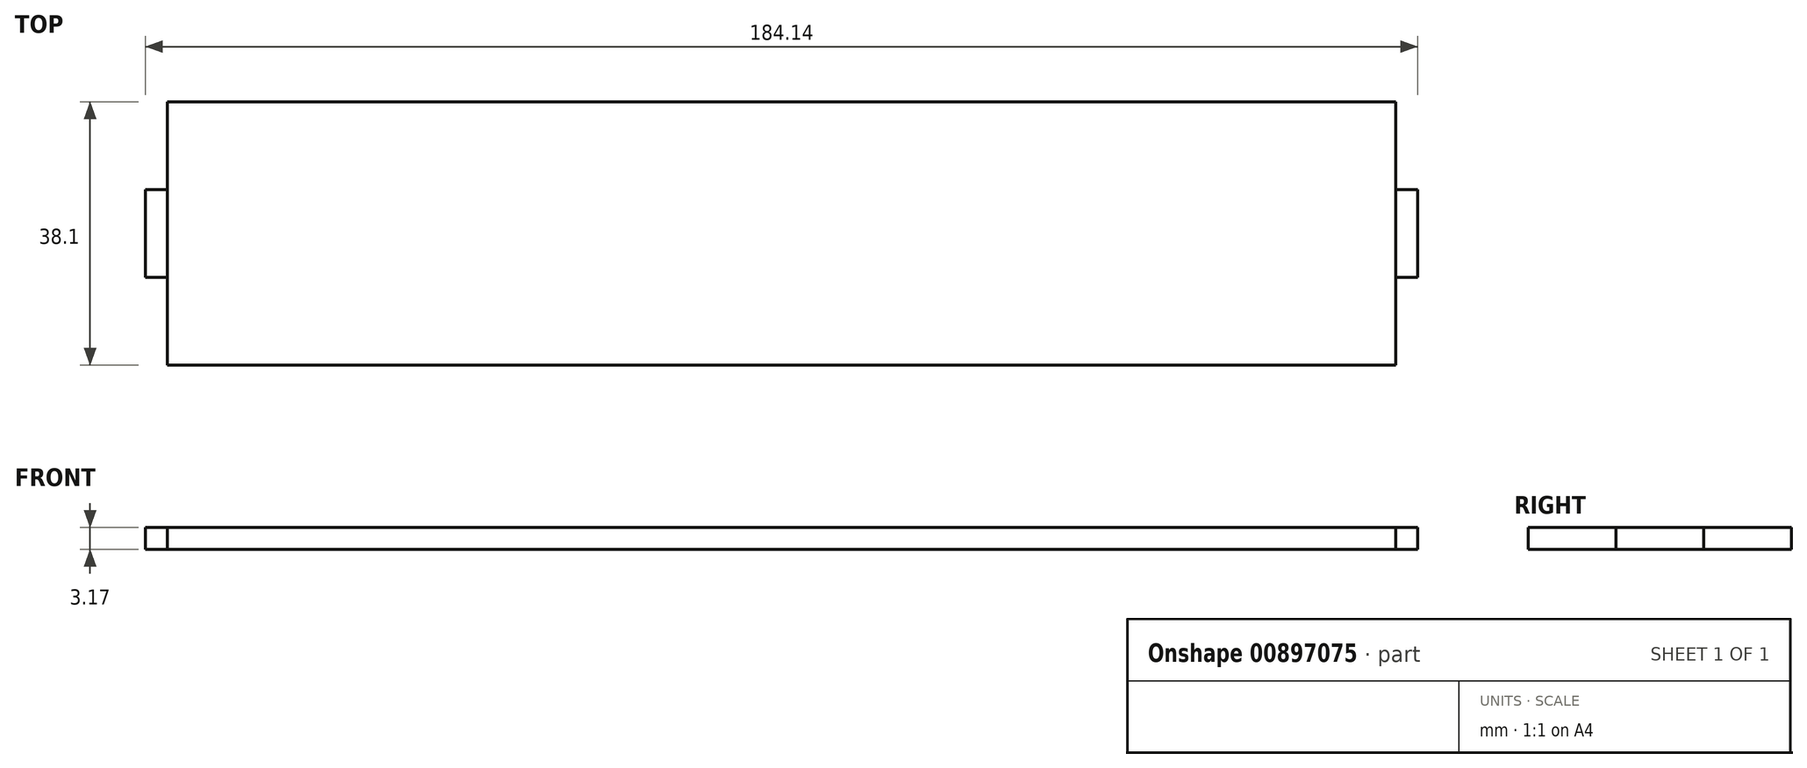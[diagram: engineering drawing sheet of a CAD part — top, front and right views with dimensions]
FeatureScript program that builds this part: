
annotation { "Feature Type Name" : "Feature", "Feature Type Description" : "" }
export const myFeature = defineFeature(function(context is Context, id is Id, definition is map)
    precondition{}
    {
        {
            var Q0;
            Q0=qCreatedBy(makeId("Top.planeOp"),FACE);
            var sketch = newSketch(context, id + "F0", { "sketchPlane" : qUnion([Q0])});
            skLineSegment(sketch, "E0.bottom", {"start": v(0, 0) * mm, "end": v(-177.8, 0) * mm});
            skLineSegment(sketch, "E0.top", {"start": v(0, -38.1) * mm, "end": v(-177.8, -38.1) * mm});
            skLineSegment(sketch, "E0.left", {"start": v(0, 0) * mm, "end": v(0, -38.1) * mm});
            skLineSegment(sketch, "E0.right", {"start": v(-177.8, 0) * mm, "end": v(-177.8, -38.1) * mm});
            skSolve(sketch);
        }
        {
            var Q0;
            Q0=makeQuery(id+"F0.imprint","IMPRINT",FACE,{"disambiguationData":[TD([[makeQuery(id+"F0.imprint","IMPRINT",EDGE,{"derivedFrom":sQuery(id+"F0.wireOp",EDGE,"E0.bottom")}),1.0]])]});
            var sketch = newSketch(context, id + "F1", { "sketchPlane" : qUnion([Q0])});
            skLineSegment(sketch, "E1.bottom", {"start": v(0, -12.7) * mm, "end": v(3.18, -12.7) * mm});
            skLineSegment(sketch, "E1.top", {"start": v(0, -25.4) * mm, "end": v(3.18, -25.4) * mm});
            skLineSegment(sketch, "E1.left", {"start": v(0, -12.7) * mm, "end": v(0, -25.4) * mm});
            skLineSegment(sketch, "E1.right", {"start": v(3.18, -12.7) * mm, "end": v(3.18, -25.4) * mm});
            skSolve(sketch);
        }
        {
            var Q0;
            {var subQ2=sQuery(id+"F1.wireOp",EDGE,"E1.left");Q0=makeQuery(id+"F1.imprint","IMPRINT",FACE,{"disambiguationData":[TD([[makeQuery(id+"F1.imprint","IMPRINT",EDGE,{"derivedFrom":subQ2}),-1.0]])]});}
            var sketch = newSketch(context, id + "F2", { "sketchPlane" : qUnion([Q0])});
            skLineSegment(sketch, "E2.bottom", {"start": v(-177.8, -25.4) * mm, "end": v(-180.98, -25.4) * mm});
            skLineSegment(sketch, "E2.top", {"start": v(-177.8, -12.7) * mm, "end": v(-180.98, -12.7) * mm});
            skLineSegment(sketch, "E2.left", {"start": v(-177.8, -25.4) * mm, "end": v(-177.8, -12.7) * mm});
            skLineSegment(sketch, "E2.right", {"start": v(-180.98, -25.4) * mm, "end": v(-180.98, -12.7) * mm});
            skSolve(sketch);
        }
        {
            var Q0;
            Q0 = qSketchRegion(id + "F0", true);
            var Q1;
            Q1 = qSketchRegion(id + "F1", true);
            var Q2;
            Q2 = qSketchRegion(id + "F2", true);
            extrude(context, id + "F3", {"entities" : qUnion([Q0, Q1, Q2]), "depth" : 3.17 * mm, "offsetDistance" : 25.4 * mm});
        }
    });
